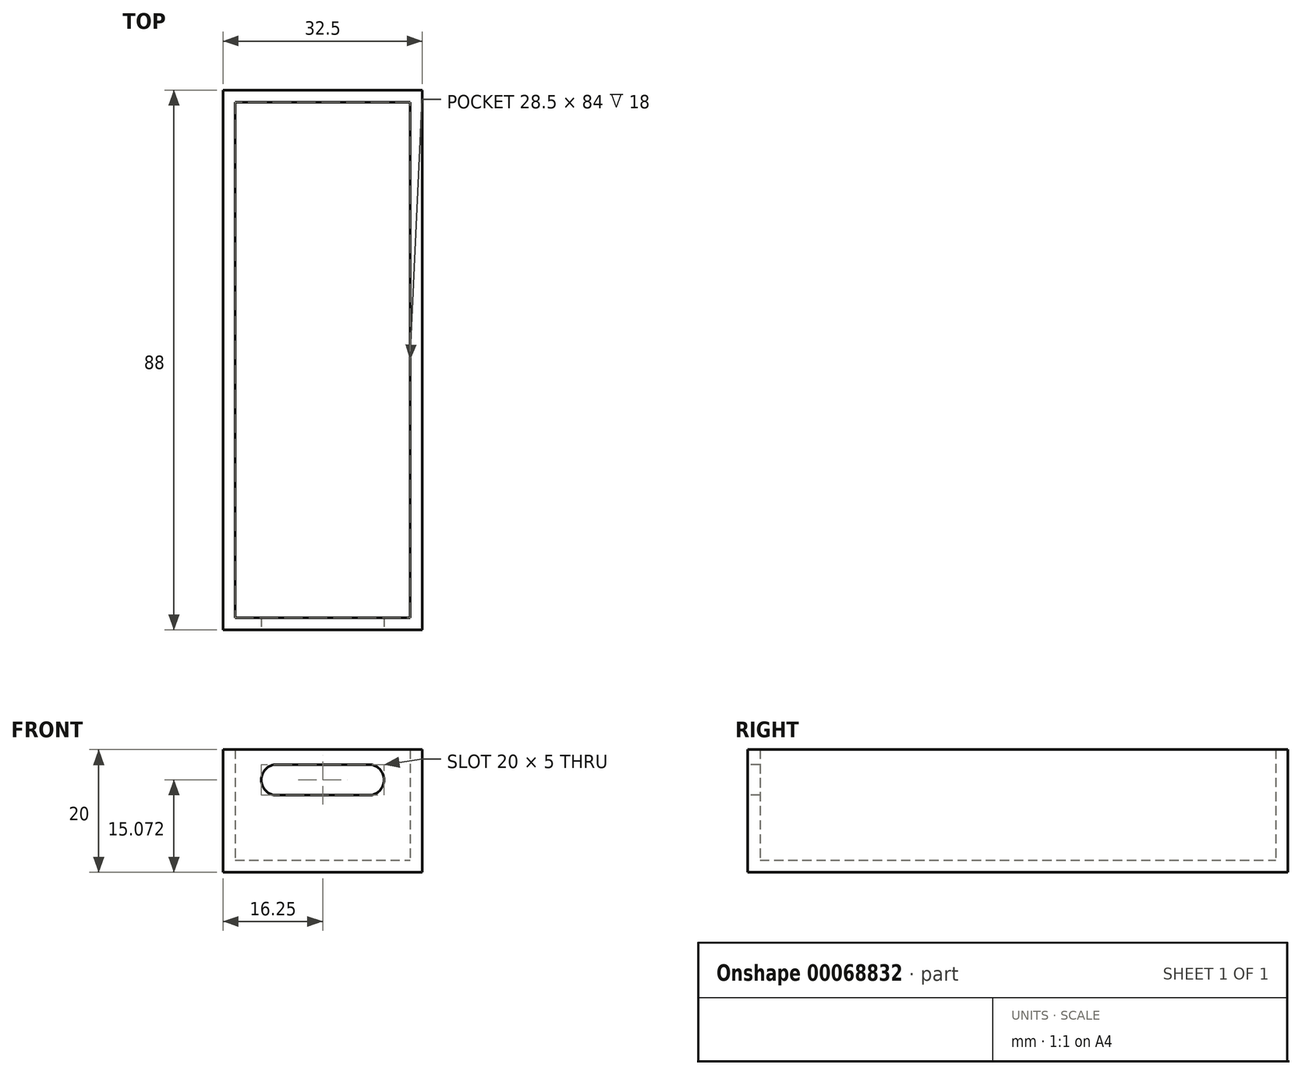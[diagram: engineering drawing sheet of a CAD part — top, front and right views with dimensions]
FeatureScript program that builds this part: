
annotation { "Feature Type Name" : "Feature", "Feature Type Description" : "" }
export const myFeature = defineFeature(function(context is Context, id is Id, definition is map)
    precondition{}
    {
        {
            var Q0;
            Q0=qCreatedBy(makeId("Front.planeOp"),FACE);
            var sketch = newSketch(context, id + "F0", { "sketchPlane" : qUnion([Q0])});
            skLineSegment(sketch, "E0.bottom", {"start": v(0, 0) * mm, "end": v(32.5, 0) * mm});
            skLineSegment(sketch, "E0.top", {"start": v(0, -20) * mm, "end": v(32.5, -20) * mm});
            skLineSegment(sketch, "E0.left", {"start": v(0, 0) * mm, "end": v(0, -20) * mm});
            skLineSegment(sketch, "E0.right", {"start": v(32.5, 0) * mm, "end": v(32.5, -20) * mm});
            skSolve(sketch);
        }
        {
            var Q0;
            Q0 = qSketchRegion(id + "F0", true);
            extrude(context, id + "F1", {"entities" : qUnion([Q0]), "depth" : 88 * mm});
        }
        {
            var Q0;
            Q0=makeQuery(id+"F1.opExtrude","SWEPT_FACE",FACE,{"disambiguationData":[OSD([sQuery(id+"F0.wireOp",EDGE,"E0.bottom")])]});
            shell(context, id + "F2", {"entities" : qUnion([Q0]), "thickness" : 2 * mm});
        }
        {
            var Q0;
            Q0=makeQuery(id+"F1.opExtrude","CAP_FACE",FACE,{"disambiguationData":[OSD([sQuery(id+"F0.wireOp",EDGE,"E0.bottom"),sQuery(id+"F0.wireOp",EDGE,"E0.top"),sQuery(id+"F0.wireOp",EDGE,"E0.left"),sQuery(id+"F0.wireOp",EDGE,"E0.right")])],"isStart":false});
            var sketch = newSketch(context, id + "F3", { "sketchPlane" : qUnion([Q0])});
            skArc(sketch, "E1", {"start": v(8.75, -2.43) * mm, "mid": v(6.25, -4.93) * mm, "end": v(8.75, -7.43) * mm});
            skArc(sketch, "E2", {"start": v(23.75, -7.43) * mm, "mid": v(26.25, -4.93) * mm, "end": v(23.75, -2.43) * mm});
            skLineSegment(sketch, "E3", {"start": v(8.75, -7.43) * mm, "end": v(23.75, -7.43) * mm});
            skLineSegment(sketch, "E4", {"start": v(8.75, -2.43) * mm, "end": v(23.75, -2.43) * mm});
            skLineSegment(sketch, "E5", {"start": v(16.25, 0) * mm, "end": v(16.25, -20) * mm, "construction": true});
            skLineSegment(sketch, "E6", {"start": v(8.75, -4.93) * mm, "end": v(23.75, -4.93) * mm, "construction": true});
            skSolve(sketch);
        }
        {
            var Q0;
            Q0=makeQuery(id+"F3.imprint","IMPRINT",FACE,{"disambiguationData":[TD([[makeQuery(id+"F3.imprint","IMPRINT",EDGE,{"derivedFrom":sQuery(id+"F3.wireOp",EDGE,"E1")}),1.0]])]});
            extrude(context, id + "F4", {"entities" : qUnion([Q0]), "operationType" : NewBodyOperationType.REMOVE, "oppositeDirection" : true, "depth" : 25 * mm});
        }
    });
